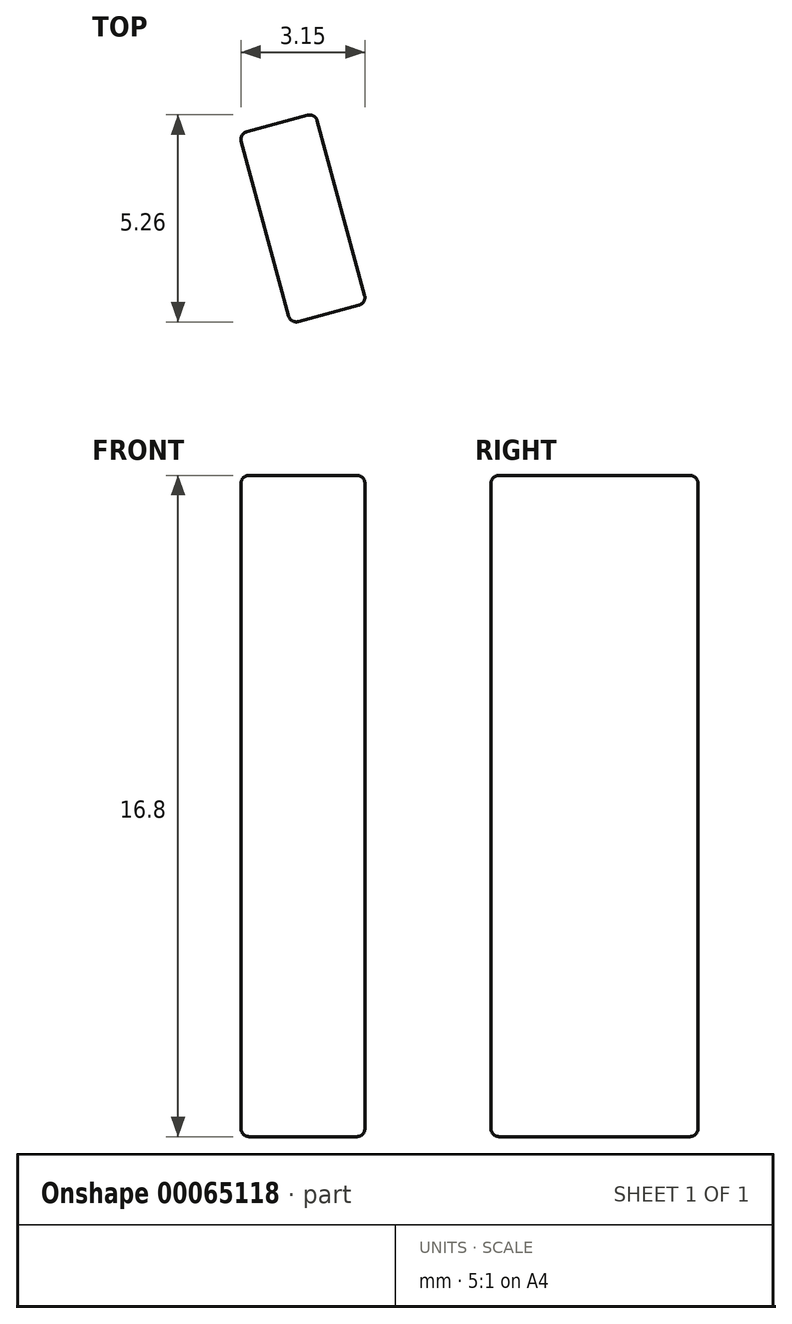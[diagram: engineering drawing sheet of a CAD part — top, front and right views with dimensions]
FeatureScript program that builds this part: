
annotation { "Feature Type Name" : "Feature", "Feature Type Description" : "" }
export const myFeature = defineFeature(function(context is Context, id is Id, definition is map)
    precondition{}
    {
        {
            var Q0;
            Q0=qCreatedBy(makeId("Top.planeOp"),FACE);
            var sketch = newSketch(context, id + "F0", { "sketchPlane" : qUnion([Q0])});
            skLineSegment(sketch, "E0", {"start": v(22.5, 2.5) * mm, "end": v(23.5, 15.5) * mm});
            skLineSegment(sketch, "E1", {"start": v(23.5, 15.5) * mm, "end": v(19, 26) * mm});
            skLineSegment(sketch, "E2", {"start": v(19, 26) * mm, "end": v(25.53, 26) * mm});
            skLineSegment(sketch, "E3", {"start": v(25.53, 26) * mm, "end": v(29.6, 16.5) * mm});
            skLineSegment(sketch, "E4", {"start": v(29.6, 16.5) * mm, "end": v(27.86, -6) * mm});
            skLineSegment(sketch, "E5", {"start": v(27.86, -6) * mm, "end": v(-27, -6) * mm});
            skLineSegment(sketch, "E6", {"start": v(-27, -6) * mm, "end": v(-36.5, 29.01) * mm});
            skLineSegment(sketch, "E7", {"start": v(-36.5, 29.01) * mm, "end": v(-36.5, 32) * mm});
            skLineSegment(sketch, "E8", {"start": v(-36.5, 32) * mm, "end": v(-18.5, 32) * mm});
            skLineSegment(sketch, "E9", {"start": v(-18.5, 32) * mm, "end": v(-18.5, 26) * mm});
            skLineSegment(sketch, "E10", {"start": v(-18.5, 26) * mm, "end": v(-23.5, 26) * mm});
            skLineSegment(sketch, "E11", {"start": v(-23.5, 26) * mm, "end": v(-26.7, 15.8) * mm});
            skLineSegment(sketch, "E12", {"start": v(-26.7, 15.8) * mm, "end": v(-23.5, 4) * mm});
            skLineSegment(sketch, "E13", {"start": v(-23.5, 4) * mm, "end": v(-19.5, 0) * mm});
            skLineSegment(sketch, "E14", {"start": v(-19.5, 0) * mm, "end": v(19.5, 0) * mm});
            skLineSegment(sketch, "E15", {"start": v(19.5, 0) * mm, "end": v(22.5, 2.5) * mm});
            skSolve(sketch);
        }
        {
            var Q0;
            Q0=qCreatedBy(makeId("Top.planeOp"),FACE);
            var sketch = newSketch(context, id + "F1", { "sketchPlane" : qUnion([Q0])});
            skLineSegment(sketch, "E16", {"start": v(22.8, 20.92) * mm, "end": v(24.65, 21.7) * mm, "construction": true});
            skLineSegment(sketch, "E17", {"start": v(24.65, 21.7) * mm, "end": v(26.62, 17.11) * mm, "construction": true});
            skLineSegment(sketch, "E18", {"start": v(26.62, 17.11) * mm, "end": v(24.78, 16.32) * mm, "construction": true});
            skLineSegment(sketch, "E19", {"start": v(24.78, 16.32) * mm, "end": v(22.8, 20.92) * mm, "construction": true});
            skLineSegment(sketch, "E20", {"start": v(-23.4, -1.5) * mm, "end": v(-18.4, -1.5) * mm, "construction": true});
            skLineSegment(sketch, "E21", {"start": v(-18.4, -1.5) * mm, "end": v(-18.4, -3.5) * mm, "construction": true});
            skLineSegment(sketch, "E22", {"start": v(-18.4, -3.5) * mm, "end": v(-23.4, -3.5) * mm, "construction": true});
            skLineSegment(sketch, "E23", {"start": v(-23.4, -3.5) * mm, "end": v(-23.4, -1.5) * mm, "construction": true});
            skLineSegment(sketch, "E24", {"start": v(-32.94, 25.42) * mm, "end": v(-31, 25.94) * mm});
            skLineSegment(sketch, "E25", {"start": v(-31, 25.94) * mm, "end": v(-29.7, 21.12) * mm});
            skLineSegment(sketch, "E26", {"start": v(-29.7, 21.12) * mm, "end": v(-31.63, 20.6) * mm});
            skLineSegment(sketch, "E27", {"start": v(-31.63, 20.6) * mm, "end": v(-32.94, 25.42) * mm});
            skLineSegment(sketch, "E28", {"start": v(-31.97, 25.68) * mm, "end": v(-30.66, 20.86) * mm, "construction": true});
            skLineSegment(sketch, "E29", {"start": v(-23.4, -2.5) * mm, "end": v(-18.4, -2.5) * mm, "construction": true});
            skLineSegment(sketch, "E30", {"start": v(25.7, 16.72) * mm, "end": v(23.73, 21.31) * mm, "construction": true});
            skLineSegment(sketch, "E31", {"start": v(-23.4, -3.5) * mm, "end": v(-27, -6) * mm, "construction": true});
            skLineSegment(sketch, "E32", {"start": v(-32.94, 25.42) * mm, "end": v(-36.5, 29.01) * mm, "construction": true});
            skLineSegment(sketch, "E33", {"start": v(24.65, 21.7) * mm, "end": v(25.53, 26) * mm, "construction": true});
            skSolve(sketch);
        }
        {
            var Q0;
            Q0=qSketchRegion(id+"F1",true);
            extrude(context, id + "F2", {"entities" : qUnion([Q0]), "depth" : 8.4 * mm});
        }
        {
            var Q0;
            Q0=makeQuery(id+"F2.opExtrude","SWEPT_BODY",BODY,{"disambiguationData":[OSD([sQuery(id+"F1.wireOp",EDGE,"E24"),sQuery(id+"F1.wireOp",EDGE,"E25"),sQuery(id+"F1.wireOp",EDGE,"E26"),sQuery(id+"F1.wireOp",EDGE,"E27")])]});
            var Q1;
            Q1=qCreatedBy(makeId("Top.planeOp"),FACE);
            mirror(context, id + "F3", {"operationType" : NewBodyOperationType.ADD, "entities" : qUnion([Q0]), "mirrorPlane" : qUnion([Q1])});
        }
        {
            var Q0;
            Q0=makeQuery(id+"F2.opExtrude","CAP_FACE",FACE,{"disambiguationData":[OSD([sQuery(id+"F1.wireOp",EDGE,"E24"),sQuery(id+"F1.wireOp",EDGE,"E25"),sQuery(id+"F1.wireOp",EDGE,"E26"),sQuery(id+"F1.wireOp",EDGE,"E27")])],"isStart":false});
            var Q1;
            {var subQ0=makeQuery(id+"F2.opExtrude","SWEPT_FACE",FACE,{"disambiguationData":[OSD([sQuery(id+"F1.wireOp",EDGE,"E26")])]});Q1=makeQuery(id+"F3.boolean.opBoolean","MERGE",FACE,{"derivedFrom":[subQ0,makeQuery(id+"F3.opPattern","COPY",FACE,{"derivedFrom":subQ0,"instanceName":"1"})]});}
            var Q2;
            {var subQ0=makeQuery(id+"F2.opExtrude","SWEPT_FACE",FACE,{"disambiguationData":[OSD([sQuery(id+"F1.wireOp",EDGE,"E24")])]});Q2=makeQuery(id+"F3.boolean.opBoolean","MERGE",FACE,{"derivedFrom":[subQ0,makeQuery(id+"F3.opPattern","COPY",FACE,{"derivedFrom":subQ0,"instanceName":"1"})]});}
            var Q3;
            Q3=makeQuery(id+"F3.opPattern","COPY",FACE,{"derivedFrom":makeQuery(id+"F2.opExtrude","CAP_FACE",FACE,{"disambiguationData":[OSD([sQuery(id+"F1.wireOp",EDGE,"E24"),sQuery(id+"F1.wireOp",EDGE,"E25"),sQuery(id+"F1.wireOp",EDGE,"E26"),sQuery(id+"F1.wireOp",EDGE,"E27")])],"isStart":false}),"instanceName":"1"});
            fillet(context, id + "F4", {"entities" : qUnion([Q0, Q1, Q2, Q3]), "radius" : .2 * mm, "tangentPropagation" : true, "allowEdgeOverflow" : false});
        }
    });
